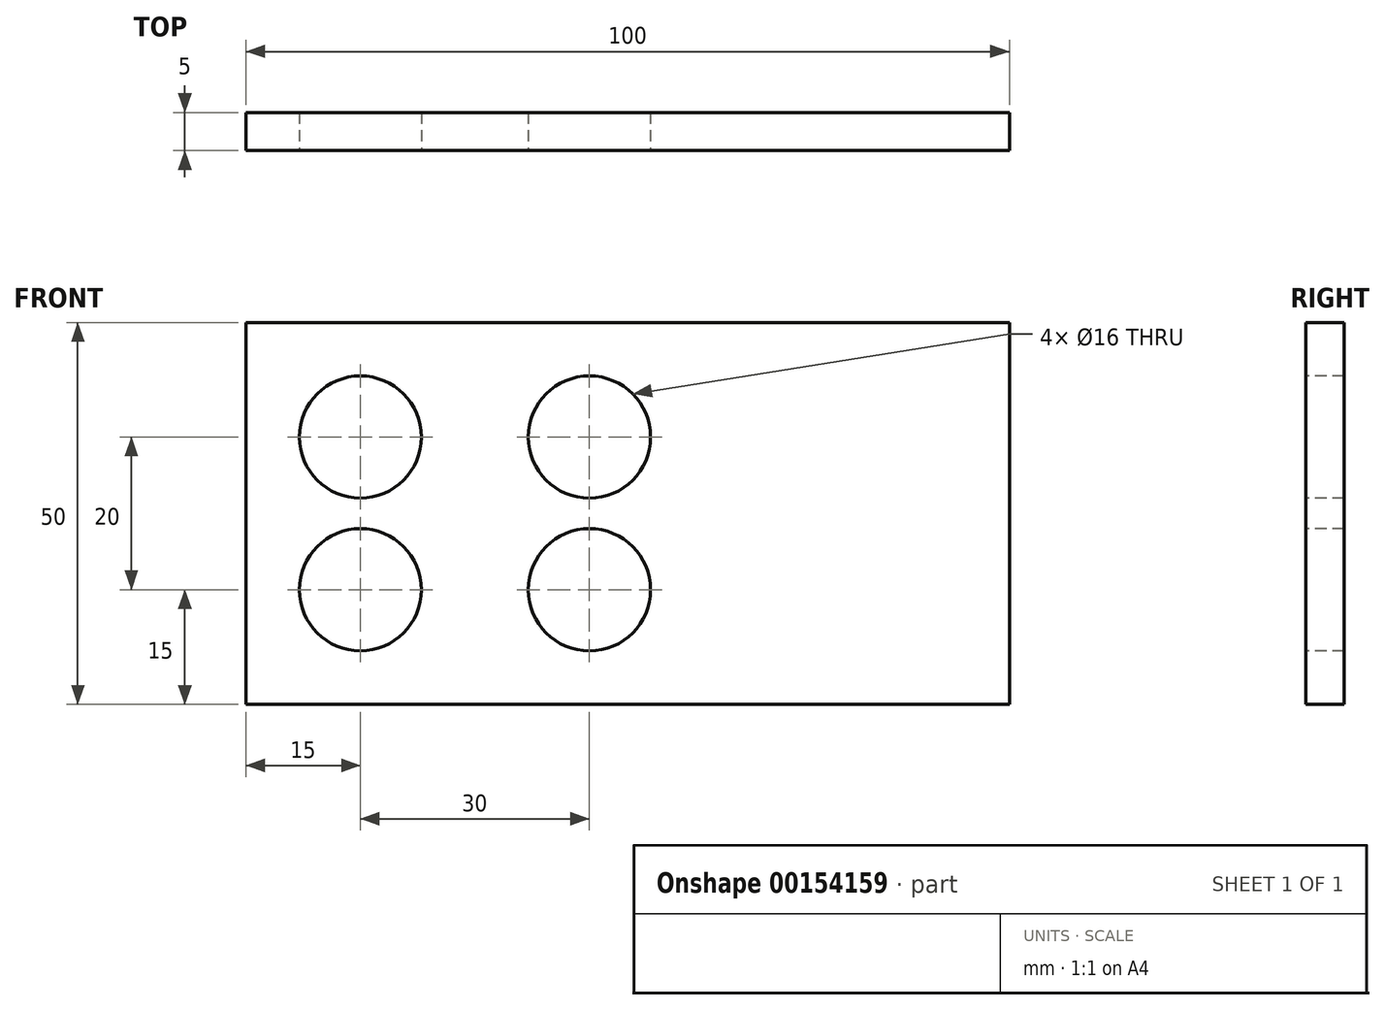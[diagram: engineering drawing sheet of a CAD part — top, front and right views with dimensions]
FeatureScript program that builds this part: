
annotation { "Feature Type Name" : "Feature", "Feature Type Description" : "" }
export const myFeature = defineFeature(function(context is Context, id is Id, definition is map)
    precondition{}
    {
        {
            var Q0;
            Q0=qCreatedBy(makeId("Front.planeOp"),FACE);
            var sketch = newSketch(context, id + "F0", { "sketchPlane" : qUnion([Q0])});
            skLineSegment(sketch, "E0.bottom", {"start": v(50, 25) * mm, "end": v(-50, 25) * mm});
            skLineSegment(sketch, "E0.top", {"start": v(50, -25) * mm, "end": v(-50, -25) * mm});
            skLineSegment(sketch, "E0.left", {"start": v(50, 25) * mm, "end": v(50, -25) * mm});
            skLineSegment(sketch, "E0.right", {"start": v(-50, 25) * mm, "end": v(-50, -25) * mm});
            skPoint(sketch, "E0.middle", {"position": v(0, 0) * mm});
            skSolve(sketch);
        }
        {
            var Q0;
            Q0=qSketchRegion(id+"F0",true);
            extrude(context, id + "F1", {"entities" : qUnion([Q0]), "depth" : 5 * mm});
        }
        {
            var Q0;
            Q0=makeQuery(id+"F1.opExtrude","CAP_FACE",FACE,{"disambiguationData":[OSD([sQuery(id+"F0.wireOp",EDGE,"E0.bottom"),sQuery(id+"F0.wireOp",EDGE,"E0.top"),sQuery(id+"F0.wireOp",EDGE,"E0.left"),sQuery(id+"F0.wireOp",EDGE,"E0.right")])],"isStart":false});
            var sketch = newSketch(context, id + "F2", { "sketchPlane" : qUnion([Q0])});
            skLineSegment(sketch, "E1.0", {"start": v(50, 25) * mm, "end": v(-50, 25) * mm});
            skLineSegment(sketch, "E2.bottom", {"start": v(-50, 25) * mm, "end": v(10, 25) * mm});
            skLineSegment(sketch, "E2.top", {"start": v(-50, -25) * mm, "end": v(10, -25) * mm});
            skLineSegment(sketch, "E2.left", {"start": v(-50, 25) * mm, "end": v(-50, -25) * mm});
            skLineSegment(sketch, "E2.right", {"start": v(10, 25) * mm, "end": v(10, -25) * mm});
            skPoint(sketch, "E3", {"position": v(-35, 10) * mm});
            skPoint(sketch, "E4", {"position": v(-5, 10) * mm});
            skPoint(sketch, "E5", {"position": v(-35, -10) * mm});
            skPoint(sketch, "E6", {"position": v(-5, -10) * mm});
            skCircle(sketch, "E7", {"center": v(-35, 10) * mm, "radius": 8 * mm});
            skCircle(sketch, "E8", {"center": v(-35, -10) * mm, "radius": 8 * mm});
            skCircle(sketch, "E9", {"center": v(-5, -10) * mm, "radius": 8 * mm});
            skCircle(sketch, "E10", {"center": v(-5, 10) * mm, "radius": 8 * mm});
            skSolve(sketch);
        }
        {
            var Q0;
            Q0=makeQuery(id+"F2.imprint","IMPRINT",FACE,{"disambiguationData":[TD([[makeQuery(id+"F2.imprint","IMPRINT",EDGE,{"derivedFrom":sQuery(id+"F2.wireOp",EDGE,"E7")}),1.0]])]});
            var Q1;
            Q1=makeQuery(id+"F2.imprint","IMPRINT",FACE,{"disambiguationData":[TD([[makeQuery(id+"F2.imprint","IMPRINT",EDGE,{"derivedFrom":sQuery(id+"F2.wireOp",EDGE,"E10")}),1.0]])]});
            var Q2;
            Q2=makeQuery(id+"F2.imprint","IMPRINT",FACE,{"disambiguationData":[TD([[makeQuery(id+"F2.imprint","IMPRINT",EDGE,{"derivedFrom":sQuery(id+"F2.wireOp",EDGE,"E9")}),1.0]])]});
            var Q3;
            Q3=makeQuery(id+"F2.imprint","IMPRINT",FACE,{"disambiguationData":[TD([[makeQuery(id+"F2.imprint","IMPRINT",EDGE,{"derivedFrom":sQuery(id+"F2.wireOp",EDGE,"E8")}),1.0]])]});
            extrude(context, id + "F3", {"entities" : qUnion([Q0, Q1, Q2, Q3]), "operationType" : NewBodyOperationType.REMOVE, "oppositeDirection" : true, "depth" : 5 * mm});
        }
    });
